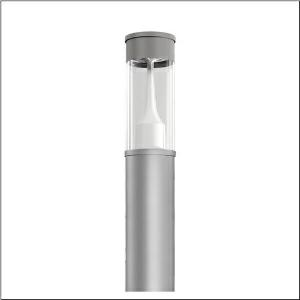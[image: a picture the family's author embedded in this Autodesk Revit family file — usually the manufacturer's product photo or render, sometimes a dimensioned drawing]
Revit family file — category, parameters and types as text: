
# Revit family: city-light_400_iq___st1_2a_5xa5305kf14hp_bbb3
name_source: partatom
category: Lighting Fixtures
units: mm (PartAtom-declared; Revit-internal decimal feet)

## family parameters
Cut with Voids When Loaded = No
Host = Face
Light Source = No
Part Type = Normal
Room Calculation Point = No
Round Connector Dimension = Use Diameter
Shared = No

## types (1)
- --- (1 x LED, 4940 lm, 33.6 W, 4000K)
    Apparent Load = 34 VA
    CIE Flux Codes = 22 61 94 96 100
    Color Rendering = 70
    Color Temperature = 4000K
    Default Elevation = 1800 mm
    Description = City-Light 400 iQ, light pillar, Module 540 iQ-SR, primary light control with 3 zone facetted reflector, of plastic, silver coated, highly specular, structured, primary optical cover: cover, of PMMA, transparent, partly coated, light distribution: ST1.2a, primary light characteristic: asymmetric, LED, High Power LED, rated luminous flux: 4.940lm, luminous efficacy: 147lm/W, light colour: 740, colour temperature: 4000K, control gear: ECG iQ, control: presetting dimming logarithmic, Street-Remote, Auto-Match, Temp-Guard, Lumen-Switch, Night-Set, Smart-Wire, Light-Fading, Desk-Remote (wireless, voltage-free reading and setting of iQ features in the workshop via application-optimized NFC function/RFID function), optimised constant luminous flux control (CLO 2.0), with terminal, 6-pole, max. 2.5mm², mains connection: 230..240V, AC, 50/60Hz, start of lifetime: 34W, end of service life: 36W, reduction: 15W, luminaire housing, cylindrical, of extruded aluminium section, coated, Siteco® metallic grey (DB 702S), length: 4.694mm, diameter: 200mm, Module 540 iQ-SR, traffic white (RAL 9016), equipment: Power, protection rating (complete): IP65, insulation class (complete): insulation class II (safety insulation), certification: CE, ENEC, VDE, packaging unit: 1 piece

Light Distribution: ST1.2a
    Height = 500 mm
    Lamp = 1 x LED
    Lamp Light Flux = 4940 lm
    Lamp Power = 33.6 W
    Lamp count = 1
    Length = 200 mm  [stored 0.656168 ft]
    Luminous efficacy = 147 lm/W
    Manufacturer = Siteco
    ModVariant = No
    Model = 5XA5305KF14HP
    Mounting Place = Floor
    Mounting Type = Freestanding
    Number of Poles = 1
    OnlyDefault = Yes
    Power Factor = 1
    Product Name = City-Light 400 iQ | ST1.2a
    Product group = light pillar
    ProductGroupID = 1303
    Protection Class = Protection class II
    Protection Degree = IP 65
    RLX_Detail_Level = 1
    RLX_Emergency_Light_Flux = 0 lm
    RLX_Emergency_Type = 0
    RLX_Emergency_Type_DB = No
    RlxData = <blob elided: 53417 chars, md5=8c12a7ff>
    Socket = socket
    Standby Power = 0 W
    System Light Flux = 4940 lm
    System Power = 34 W
    Type Comments = factory setting: luminous flux: 100 % | dim-lin: 254 | 695 mA
    Type Image = l_1006916.jpg
    URL = http://relux.com
    VarID = @adj_145467
    Voltage = 0 V
    Weight = 0.00 kg
    Width = 0 mm  [stored 0 ft]

note: [stored X ft] marks values corroborated as IEEE doubles in the binary element streams (Revit-internal decimal feet)

## geometry (parser evidence)
native form markers: Blend x4, Sweep x10
no freeform markers — native parametric forms only
